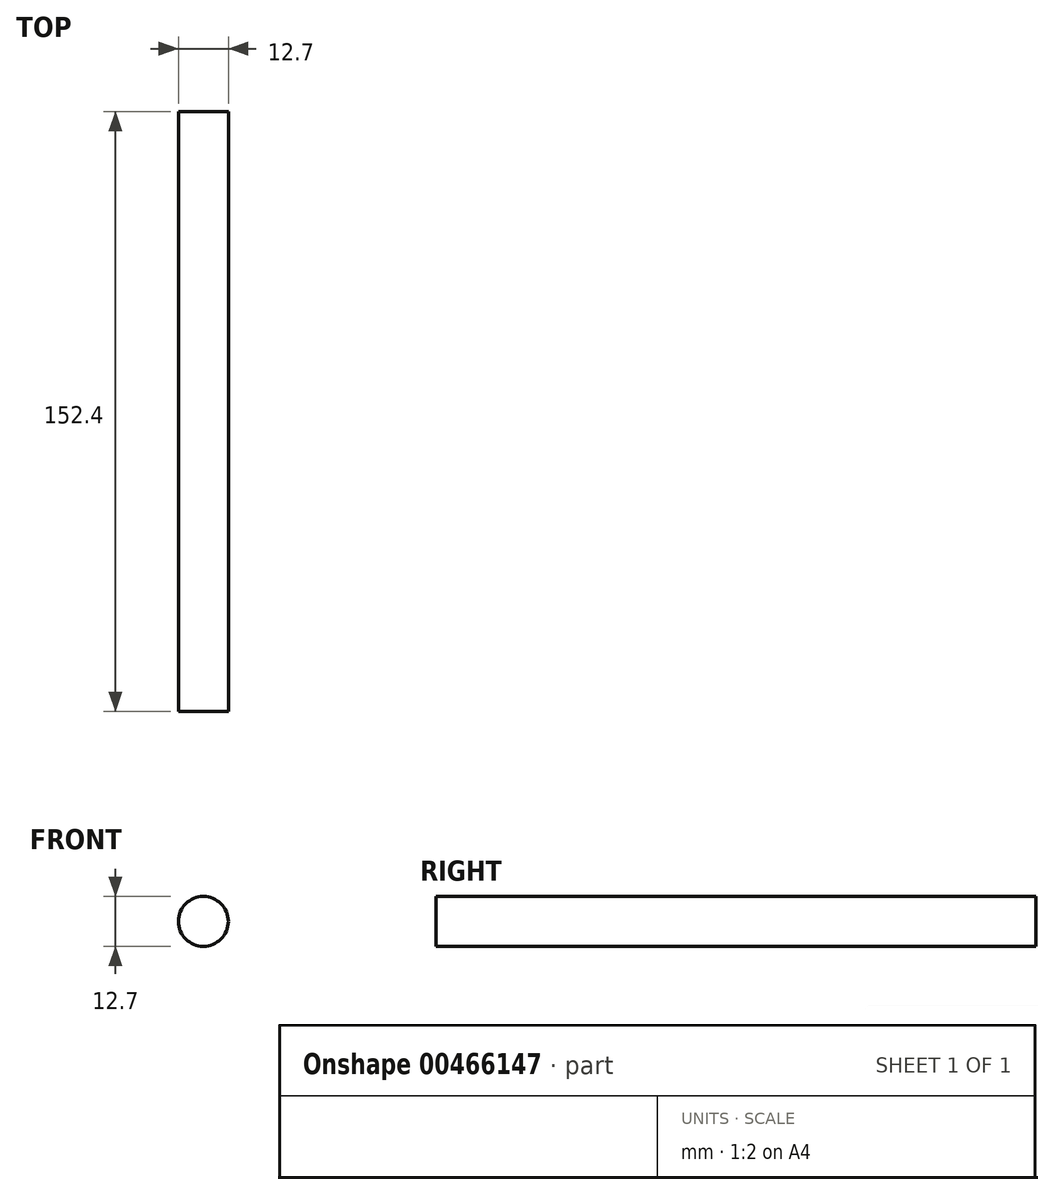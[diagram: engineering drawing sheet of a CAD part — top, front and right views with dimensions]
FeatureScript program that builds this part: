
annotation { "Feature Type Name" : "Feature", "Feature Type Description" : "" }
export const myFeature = defineFeature(function(context is Context, id is Id, definition is map)
    precondition{}
    {
        {
            var Q0;
            Q0=qCreatedBy(makeId("Front.planeOp"),FACE);
            var sketch = newSketch(context, id + "F0", { "sketchPlane" : qUnion([Q0])});
            skCircle(sketch, "E0", {"center": v(0, 0) * mm, "radius": 6.35 * mm});
            skSolve(sketch);
        }
        {
            var Q0;
            Q0 = qSketchRegion(id + "F0", true);
            extrude(context, id + "F1", {"entities" : qUnion([Q0]), "endBound" : BoundingType.SYMMETRIC, "depth" : 152.4 * mm});
        }
    });
